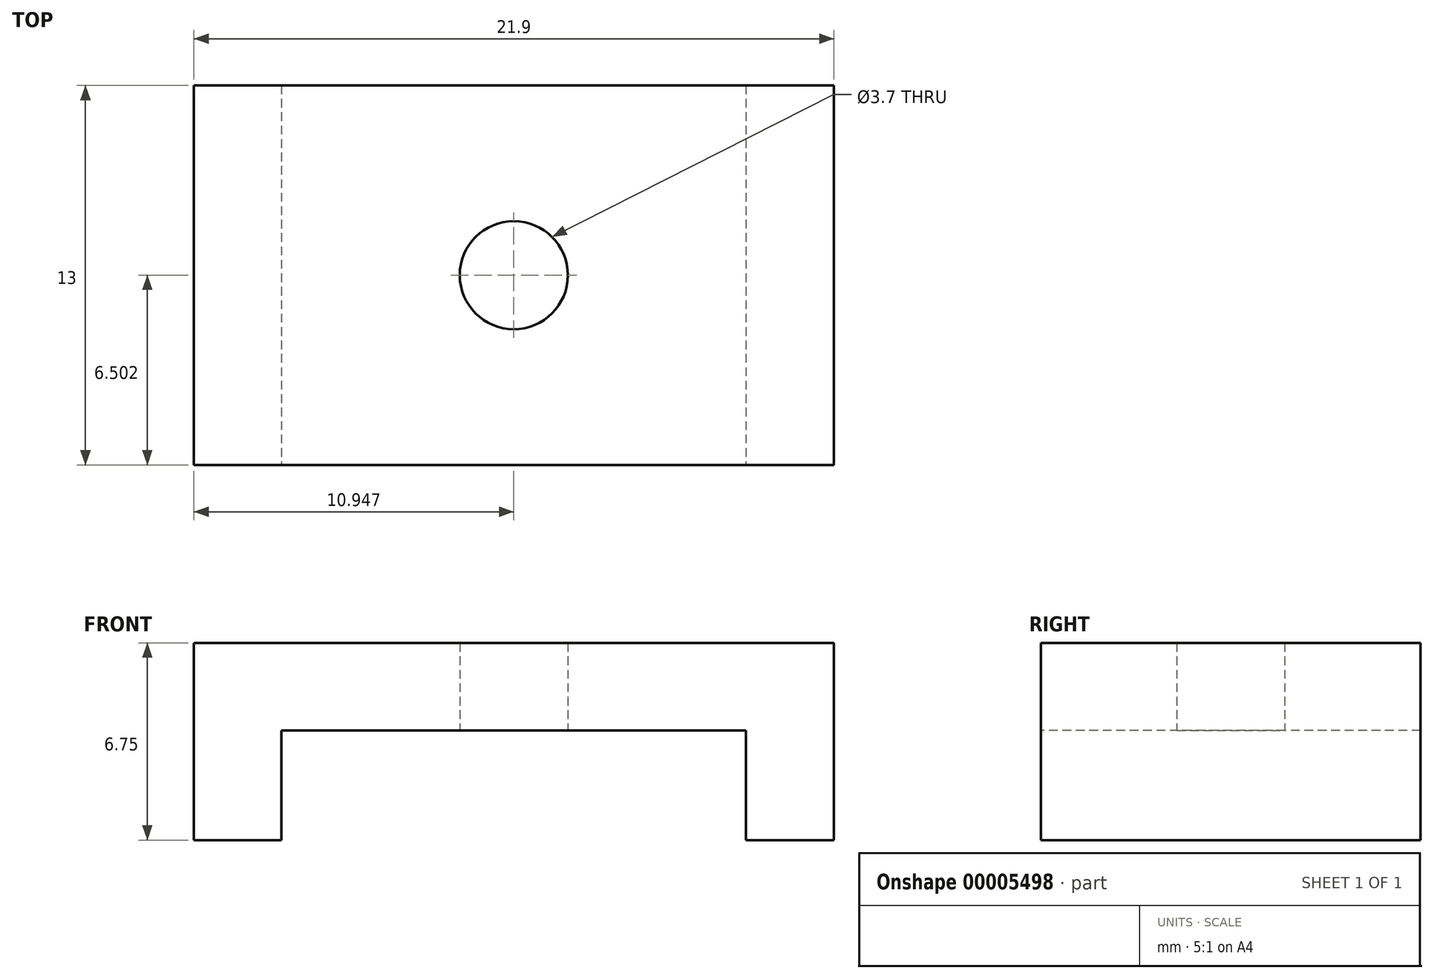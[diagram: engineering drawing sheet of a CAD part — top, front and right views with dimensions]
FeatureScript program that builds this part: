
annotation { "Feature Type Name" : "Feature", "Feature Type Description" : "" }
export const myFeature = defineFeature(function(context is Context, id is Id, definition is map)
    precondition{}
    {
        {
            var Q0;
            Q0=qCreatedBy(makeId("Top.planeOp"),FACE);
            var sketch = newSketch(context, id + "F0", { "sketchPlane" : qUnion([Q0])});
            skLineSegment(sketch, "E0.bottom", {"start": v(-6.93, 24.15) * mm, "end": v(8.97, 24.15) * mm});
            skLineSegment(sketch, "E0.top", {"start": v(-6.93, 11.15) * mm, "end": v(8.97, 11.15) * mm});
            skLineSegment(sketch, "E1", {"start": v(1.02, 24.15) * mm, "end": v(1.02, 11.15) * mm, "construction": true});
            skCircle(sketch, "E2", {"center": v(1.02, 17.65) * mm, "radius": 1.85 * mm});
            skCircle(sketch, "E3", {"center": v(1.02, 17.65) * mm, "radius": 6.5 * mm, "construction": true});
            skLineSegment(sketch, "E4", {"start": v(-6.93, 24.15) * mm, "end": v(-9.93, 24.15) * mm});
            skLineSegment(sketch, "E5", {"start": v(-9.93, 24.15) * mm, "end": v(-9.93, 11.15) * mm});
            skLineSegment(sketch, "E6", {"start": v(-6.93, 11.15) * mm, "end": v(-9.93, 11.15) * mm});
            skLineSegment(sketch, "E7", {"start": v(8.97, 24.15) * mm, "end": v(11.97, 24.15) * mm});
            skLineSegment(sketch, "E8", {"start": v(8.97, 11.15) * mm, "end": v(11.97, 11.15) * mm});
            skLineSegment(sketch, "E9", {"start": v(11.97, 24.15) * mm, "end": v(11.97, 11.15) * mm});
            skSolve(sketch);
        }
        {
            var Q0;
            Q0=qSketchRegion(id+"F0",true);
            extrude(context, id + "F1", {"entities" : qUnion([Q0]), "depth" : 2.4 * mm});
        }
        {
            var Q0;
            Q0=makeQuery(id+"F1.opExtrude","CAP_FACE",FACE,{"disambiguationData":[OSD([sQuery(id+"F0.wireOp",EDGE,"E0.bottom"),sQuery(id+"F0.wireOp",EDGE,"E0.top"),sQuery(id+"F0.wireOp",EDGE,"E2"),sQuery(id+"F0.wireOp",EDGE,"E4"),sQuery(id+"F0.wireOp",EDGE,"E5"),sQuery(id+"F0.wireOp",EDGE,"E6"),sQuery(id+"F0.wireOp",EDGE,"E7"),sQuery(id+"F0.wireOp",EDGE,"E8"),sQuery(id+"F0.wireOp",EDGE,"E9")])],"isStart":false});
            var sketch = newSketch(context, id + "F2", { "sketchPlane" : qUnion([Q0])});
            skLineSegment(sketch, "E10.bottom", {"start": v(-9.93, 24.15) * mm, "end": v(-6.93, 24.15) * mm});
            skLineSegment(sketch, "E10.top", {"start": v(-9.93, 11.15) * mm, "end": v(-6.93, 11.15) * mm});
            skLineSegment(sketch, "E10.left", {"start": v(-9.93, 24.15) * mm, "end": v(-9.93, 11.15) * mm});
            skLineSegment(sketch, "E10.right", {"start": v(-6.93, 24.15) * mm, "end": v(-6.93, 11.15) * mm});
            skLineSegment(sketch, "E11.bottom", {"start": v(11.97, 24.15) * mm, "end": v(8.97, 24.15) * mm});
            skLineSegment(sketch, "E11.top", {"start": v(11.97, 11.15) * mm, "end": v(8.97, 11.15) * mm});
            skLineSegment(sketch, "E11.left", {"start": v(11.97, 24.15) * mm, "end": v(11.97, 11.15) * mm});
            skLineSegment(sketch, "E11.right", {"start": v(8.97, 24.15) * mm, "end": v(8.97, 11.15) * mm});
            skSolve(sketch);
        }
        {
            var Q0;
            Q0=qSketchRegion(id+"F2",true);
            extrude(context, id + "F3", {"entities" : qUnion([Q0]), "operationType" : NewBodyOperationType.ADD, "depth" : 3.75 * mm});
        }
        {
            var Q0;
            Q0=makeQuery(id+"F1.opExtrude","CAP_FACE",FACE,{"disambiguationData":[OSD([sQuery(id+"F0.wireOp",EDGE,"E0.bottom"),sQuery(id+"F0.wireOp",EDGE,"E0.top"),sQuery(id+"F0.wireOp",EDGE,"E2"),sQuery(id+"F0.wireOp",EDGE,"E4"),sQuery(id+"F0.wireOp",EDGE,"E5"),sQuery(id+"F0.wireOp",EDGE,"E6"),sQuery(id+"F0.wireOp",EDGE,"E7"),sQuery(id+"F0.wireOp",EDGE,"E8"),sQuery(id+"F0.wireOp",EDGE,"E9")])],"isStart":true});
            var sketch = newSketch(context, id + "F4", { "sketchPlane" : qUnion([Q0])});
            skCircle(sketch, "E12", {"center": v(1.02, -17.65) * mm, "radius": 6.5 * mm});
            skSolve(sketch);
        }
        {
            var Q0;
            Q0=makeQuery(id+"F3.boolean.opBoolean","MERGE",FACE,{"derivedFrom":[makeQuery(id+"F1.opExtrude","SWEPT_FACE",FACE,{"disambiguationData":[OSD([sQuery(id+"F0.wireOp",EDGE,"E5")])]}),makeQuery(id+"F3.opExtrude","SWEPT_FACE",FACE,{"disambiguationData":[OSD([sQuery(id+"F2.wireOp",EDGE,"E10.left")])]})]});
            var sketch = newSketch(context, id + "F5", { "sketchPlane" : qUnion([Q0])});
            skLineSegment(sketch, "E13.0", {"start": v(-11.15, -5) * mm, "end": v(-24.15, -5) * mm, "construction": true});
            skLineSegment(sketch, "E14.0", {"start": v(-11.15, 0) * mm, "end": v(-24.15, 0) * mm, "construction": true});
            skLineSegment(sketch, "E15", {"start": v(-24.15, -2.5) * mm, "end": v(-24.15, -5) * mm, "construction": true});
            skLineSegment(sketch, "E16", {"start": v(-24.15, -2.5) * mm, "end": v(-29.8, -2.5) * mm, "construction": true});
            skArc(sketch, "E17", {"start": v(-24.23, 0) * mm, "mid": v(-21.02, -5.55) * mm, "end": v(-22.22, 0.75) * mm});
            skLineSegment(sketch, "E18", {"start": v(-22.09, 0.75) * mm, "end": v(-25.9, 0.75) * mm});
            skLineSegment(sketch, "E19", {"start": v(-25.9, 0.75) * mm, "end": v(-25.9, 0) * mm});
            skLineSegment(sketch, "E20", {"start": v(-25.9, 0) * mm, "end": v(-24.23, 0) * mm});
            skSolve(sketch);
        }
        {
            var Q0;
            Q0=qSketchRegion(id+"F5",true);
            extrude(context, id + "F6", {"entities" : qUnion([Q0]), "operationType" : NewBodyOperationType.REMOVE, "oppositeDirection" : true, "depth" : 25 * mm});
        }
        {
            var Q0;
            Q0=makeQuery(id+"F3.opExtrude","CAP_FACE",FACE,{"disambiguationData":[OSD([sQuery(id+"F2.wireOp",EDGE,"E11.bottom"),sQuery(id+"F2.wireOp",EDGE,"E11.top"),sQuery(id+"F2.wireOp",EDGE,"E11.left"),sQuery(id+"F2.wireOp",EDGE,"E11.right")])],"isStart":false});
            var sketch = newSketch(context, id + "F7", { "sketchPlane" : qUnion([Q0])});
            skLineSegment(sketch, "E21.0", {"start": v(-9.93, 24.15) * mm, "end": v(-9.93, 11.15) * mm});
            skLineSegment(sketch, "E22.0", {"start": v(11.97, 24.15) * mm, "end": v(11.97, 11.15) * mm});
            skLineSegment(sketch, "E23", {"start": v(-9.93, 11.15) * mm, "end": v(11.97, 11.15) * mm});
            skLineSegment(sketch, "E24", {"start": v(11.97, 24.15) * mm, "end": v(-9.93, 24.15) * mm});
            skSolve(sketch);
        }
        {
            var Q0;
            Q0=qSketchRegion(id+"F7",true);
            extrude(context, id + "F8", {"entities" : qUnion([Q0]), "operationType" : NewBodyOperationType.ADD, "depth" : 3 * mm});
        }
        {
            var Q0;
            Q0=makeQuery(id+"F8.opExtrude","CAP_FACE",FACE,{"disambiguationData":[OSD([sQuery(id+"F7.wireOp",EDGE,"E21.0"),sQuery(id+"F7.wireOp",EDGE,"E22.0"),sQuery(id+"F7.wireOp",EDGE,"E23"),sQuery(id+"F7.wireOp",EDGE,"E24")])],"isStart":true});
            var sketch = newSketch(context, id + "F9", { "sketchPlane" : qUnion([Q0])});
            skCircle(sketch, "E25.0", {"center": v(1.02, -17.65) * mm, "radius": 1.85 * mm});
            skSolve(sketch);
        }
        {
            var Q0;
            Q0=qSketchRegion(id+"F9",true);
            extrude(context, id + "F10", {"entities" : qUnion([Q0]), "operationType" : NewBodyOperationType.REMOVE, "oppositeDirection" : true, "depth" : 25 * mm});
        }
        {
            var Q0;
            Q0=makeQuery(id+"F8.boolean.opBoolean","MERGE",FACE,{"derivedFrom":[makeQuery(id+"F3.boolean.opBoolean","MERGE",FACE,{"derivedFrom":[makeQuery(id+"F1.opExtrude","SWEPT_FACE",FACE,{"disambiguationData":[OSD([sQuery(id+"F0.wireOp",EDGE,"E9")])]}),makeQuery(id+"F3.opExtrude","SWEPT_FACE",FACE,{"disambiguationData":[OSD([sQuery(id+"F2.wireOp",EDGE,"E11.left")])]})]}),makeQuery(id+"F8.opExtrude","SWEPT_FACE",FACE,{"disambiguationData":[OSD([sQuery(id+"F7.wireOp",EDGE,"E22.0")])]})]});
            var sketch = newSketch(context, id + "F11", { "sketchPlane" : qUnion([Q0])});
            skLineSegment(sketch, "E26.0", {"start": v(24.15, 0) * mm, "end": v(11.15, 0) * mm});
            skLineSegment(sketch, "E27", {"start": v(11.15, 0) * mm, "end": v(11.15, 0.8) * mm});
            skLineSegment(sketch, "E28", {"start": v(11.15, 0.8) * mm, "end": v(24.15, 0.8) * mm});
            skLineSegment(sketch, "E29", {"start": v(24.15, 0.8) * mm, "end": v(24.15, 0) * mm});
            skSolve(sketch);
        }
        {
            var Q0;
            Q0=qSketchRegion(id+"F11",true);
            extrude(context, id + "F12", {"entities" : qUnion([Q0]), "operationType" : NewBodyOperationType.REMOVE, "oppositeDirection" : true, "depth" : 25 * mm});
        }
        {
            var Q0;
            Q0=makeQuery(id+"F12.boolean.opBoolean","COPY",FACE,{"derivedFrom":makeQuery(id+"F12.opExtrude","SWEPT_FACE",FACE,{"disambiguationData":[OSD([sQuery(id+"F11.wireOp",EDGE,"E28")])]})});
            var sketch = newSketch(context, id + "F13", { "sketchPlane" : qUnion([Q0])});
            skLineSegment(sketch, "E30.0", {"start": v(-9.93, -24.15) * mm, "end": v(11.97, -24.15) * mm});
            skLineSegment(sketch, "E31", {"start": v(-9.93, -24.15) * mm, "end": v(-9.93, -4.15) * mm});
            skLineSegment(sketch, "E32", {"start": v(-9.93, -4.15) * mm, "end": v(11.97, -4.15) * mm});
            skLineSegment(sketch, "E33", {"start": v(11.97, -24.15) * mm, "end": v(11.97, -4.15) * mm});
            skSolve(sketch);
        }
        {
            var Q0;
            Q0=qSketchRegion(id+"F13",true);
            var Q1;
            Q1=makeQuery(id+"F1.opExtrude","CAP_FACE",FACE,{"disambiguationData":[OSD([sQuery(id+"F0.wireOp",EDGE,"E0.bottom"),sQuery(id+"F0.wireOp",EDGE,"E0.top"),sQuery(id+"F0.wireOp",EDGE,"E2"),sQuery(id+"F0.wireOp",EDGE,"E4"),sQuery(id+"F0.wireOp",EDGE,"E5"),sQuery(id+"F0.wireOp",EDGE,"E6"),sQuery(id+"F0.wireOp",EDGE,"E7"),sQuery(id+"F0.wireOp",EDGE,"E8"),sQuery(id+"F0.wireOp",EDGE,"E9")])],"isStart":false});
            extrude(context, id + "F14", {"entities" : qUnion([Q0]), "operationType" : NewBodyOperationType.REMOVE, "endBound" : BoundingType.UP_TO_SURFACE, "oppositeDirection" : true, "endBoundEntityFace" : qUnion([Q1]), "depth" : 1.6 * mm});
        }
    });
